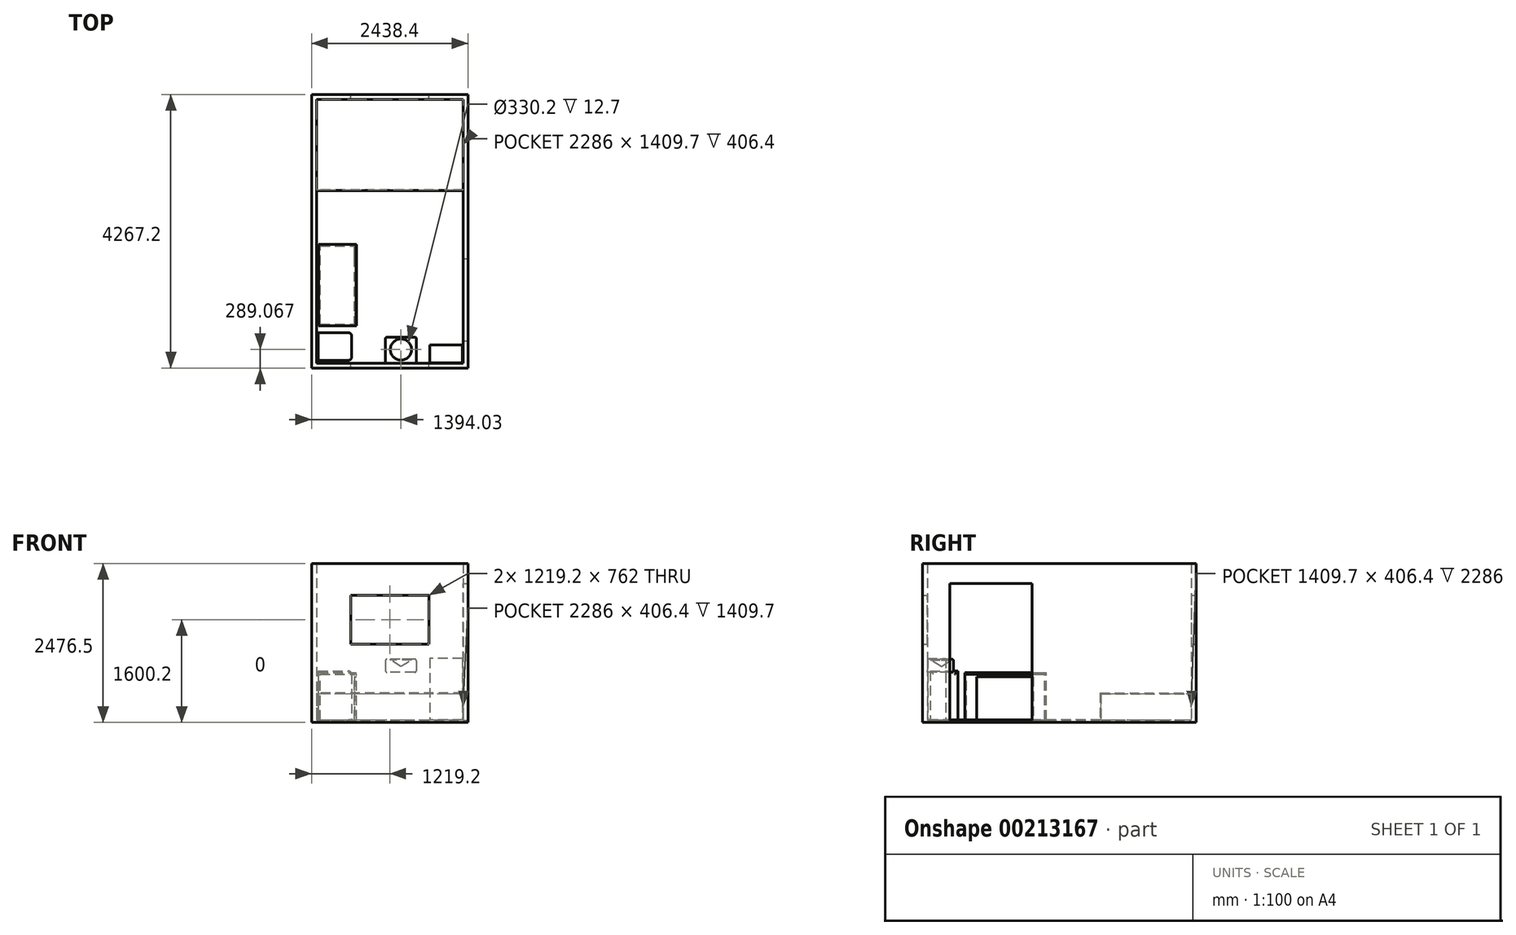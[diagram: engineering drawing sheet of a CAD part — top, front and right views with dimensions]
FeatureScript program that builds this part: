
annotation { "Feature Type Name" : "Feature", "Feature Type Description" : "" }
export const myFeature = defineFeature(function(context is Context, id is Id, definition is map)
    precondition{}
    {
        {
            var Q0;
            Q0=qCreatedBy(makeId("Top.planeOp"),FACE);
            var sketch = newSketch(context, id + "F0", { "sketchPlane" : qUnion([Q0])});
            skLineSegment(sketch, "E0.bottom", {"start": v(0, 0) * mm, "end": v(2438.4, 0) * mm});
            skLineSegment(sketch, "E0.top", {"start": v(0, 4267.2) * mm, "end": v(2438.4, 4267.2) * mm});
            skLineSegment(sketch, "E0.left", {"start": v(0, 0) * mm, "end": v(0, 4267.2) * mm});
            skLineSegment(sketch, "E0.right", {"start": v(2438.4, 0) * mm, "end": v(2438.4, 4267.2) * mm});
            skSolve(sketch);
        }
        {
            var Q0;
            Q0=makeQuery(id+"F0.imprint","IMPRINT",FACE,{"disambiguationData":[TD([[makeQuery(id+"F0.imprint","IMPRINT",EDGE,{"derivedFrom":sQuery(id+"F0.wireOp",EDGE,"E0.bottom")}),1.0]])]});
            extrude(context, id + "F1", {"entities" : qUnion([Q0]), "depth" : 38.1 * mm});
        }
        {
            var Q0;
            Q0=makeQuery(id+"F1.opExtrude","CAP_FACE",FACE,{"disambiguationData":[OSD([sQuery(id+"F0.wireOp",EDGE,"E0.bottom"),sQuery(id+"F0.wireOp",EDGE,"E0.top"),sQuery(id+"F0.wireOp",EDGE,"E0.left"),sQuery(id+"F0.wireOp",EDGE,"E0.right")])],"isStart":false});
            var sketch = newSketch(context, id + "F2", { "sketchPlane" : qUnion([Q0])});
            skLineSegment(sketch, "E1.bottom", {"start": v(0, 0) * mm, "end": v(2438.4, 0) * mm});
            skLineSegment(sketch, "E1.top", {"start": v(76.2, 76.2) * mm, "end": v(2362.2, 76.2) * mm});
            skLineSegment(sketch, "E1.left", {"start": v(0, 0) * mm, "end": v(0, 76.2) * mm});
            skLineSegment(sketch, "E1.right", {"start": v(2438.4, 0) * mm, "end": v(2438.4, 76.2) * mm});
            skLineSegment(sketch, "E2.bottom", {"start": v(2438.4, 0) * mm, "end": v(2362.2, 0) * mm});
            skLineSegment(sketch, "E2.top", {"start": v(2438.4, 4267.2) * mm, "end": v(2362.2, 4267.2) * mm});
            skLineSegment(sketch, "E2.left", {"start": v(2438.4, 0) * mm, "end": v(2438.4, 4267.2) * mm});
            skLineSegment(sketch, "E2.right", {"start": v(2362.2, 76.2) * mm, "end": v(2362.2, 4191) * mm});
            skLineSegment(sketch, "E3.bottom", {"start": v(2438.4, 4267.2) * mm, "end": v(0, 4267.2) * mm});
            skLineSegment(sketch, "E3.top", {"start": v(2362.2, 4191) * mm, "end": v(76.2, 4191) * mm});
            skLineSegment(sketch, "E3.left", {"start": v(2438.4, 4267.2) * mm, "end": v(2438.4, 4191) * mm});
            skLineSegment(sketch, "E3.right", {"start": v(0, 4267.2) * mm, "end": v(0, 4191) * mm});
            skLineSegment(sketch, "E4.bottom", {"start": v(0, 4267.2) * mm, "end": v(76.2, 4267.2) * mm});
            skLineSegment(sketch, "E4.top", {"start": v(0, 0) * mm, "end": v(76.2, 0) * mm});
            skLineSegment(sketch, "E4.left", {"start": v(0, 4267.2) * mm, "end": v(0, 0) * mm});
            skLineSegment(sketch, "E4.right", {"start": v(76.2, 4191) * mm, "end": v(76.2, 76.2) * mm});
            skSolve(sketch);
        }
        {
            var Q0;
            Q0=makeQuery(id+"F2.imprint","IMPRINT",FACE,{"disambiguationData":[TD([[makeQuery(id+"F2.imprint","IMPRINT",EDGE,{"derivedFrom":sQuery(id+"F2.wireOp",EDGE,"E1.bottom")}),1.0]])]});
            extrude(context, id + "F3", {"entities" : qUnion([Q0]), "operationType" : NewBodyOperationType.ADD, "depth" : 2438.4 * mm});
        }
        {
            var Q0;
            Q0=makeQuery(id+"F3.boolean.opBoolean","MERGE",FACE,{"derivedFrom":[makeQuery(id+"F1.opExtrude","SWEPT_FACE",FACE,{"disambiguationData":[OSD([sQuery(id+"F0.wireOp",EDGE,"E0.right")])]}),makeQuery(id+"F3.opExtrude","SWEPT_FACE",FACE,{"disambiguationData":[OSD([sQuery(id+"F2.wireOp",EDGE,"E2.left"),sQuery(id+"F2.wireOp",EDGE,"E3.left")])]})]});
            var sketch = newSketch(context, id + "F4", { "sketchPlane" : qUnion([Q0])});
            skLineSegment(sketch, "E5.bottom", {"start": v(0, 0) * mm, "end": v(422.77, 0) * mm});
            skLineSegment(sketch, "E5.left", {"start": v(0, 0) * mm, "end": v(0, 35.23) * mm});
            skLineSegment(sketch, "E6.bottom", {"start": v(422.77, 35.23) * mm, "end": v(1708.3, 35.23) * mm});
            skLineSegment(sketch, "E6.top", {"start": v(422.77, 2168.83) * mm, "end": v(1708.3, 2168.83) * mm});
            skLineSegment(sketch, "E6.left", {"start": v(422.77, 35.23) * mm, "end": v(422.77, 2168.83) * mm});
            skLineSegment(sketch, "E6.right", {"start": v(1708.3, 35.23) * mm, "end": v(1708.3, 2168.83) * mm});
            skSolve(sketch);
        }
        {
            var Q0;
            Q0 = qSketchRegion(id + "F4", true);
            extrude(context, id + "F5", {"entities" : qUnion([Q0]), "operationType" : NewBodyOperationType.REMOVE, "oppositeDirection" : true, "depth" : 76.2 * mm});
        }
        {
            var Q0;
            Q0=makeQuery(id+"F3.boolean.opBoolean","MERGE",FACE,{"derivedFrom":[makeQuery(id+"F1.opExtrude","SWEPT_FACE",FACE,{"disambiguationData":[OSD([sQuery(id+"F0.wireOp",EDGE,"E0.top")])]}),makeQuery(id+"F3.opExtrude","SWEPT_FACE",FACE,{"disambiguationData":[OSD([sQuery(id+"F2.wireOp",EDGE,"E3.bottom"),sQuery(id+"F2.wireOp",EDGE,"E4.bottom")])]})]});
            var sketch = newSketch(context, id + "F6", { "sketchPlane" : qUnion([Q0])});
            skLineSegment(sketch, "E7.bottom", {"start": v(-1828.8, 1219.2) * mm, "end": v(-609.6, 1219.2) * mm});
            skLineSegment(sketch, "E7.top", {"start": v(-1828.8, 1981.2) * mm, "end": v(-609.6, 1981.2) * mm});
            skLineSegment(sketch, "E7.left", {"start": v(-1828.8, 1219.2) * mm, "end": v(-1828.8, 1981.2) * mm});
            skLineSegment(sketch, "E7.right", {"start": v(-609.6, 1219.2) * mm, "end": v(-609.6, 1981.2) * mm});
            skSolve(sketch);
        }
        {
            var Q0;
            Q0 = qSketchRegion(id + "F6", true);
            extrude(context, id + "F7", {"entities" : qUnion([Q0]), "operationType" : NewBodyOperationType.REMOVE, "oppositeDirection" : true, "depth" : 4996.18 * mm});
        }
        {
            var Q0;
            Q0=makeQuery(id+"F1.opExtrude","CAP_FACE",FACE,{"disambiguationData":[OSD([sQuery(id+"F0.wireOp",EDGE,"E0.bottom"),sQuery(id+"F0.wireOp",EDGE,"E0.top"),sQuery(id+"F0.wireOp",EDGE,"E0.left"),sQuery(id+"F0.wireOp",EDGE,"E0.right")])],"isStart":false});
            var sketch = newSketch(context, id + "F8", { "sketchPlane" : qUnion([Q0])});
            skLineSegment(sketch, "E8", {"start": v(76.2, 4191) * mm, "end": v(76.2, 2768.6) * mm});
            skLineSegment(sketch, "E9", {"start": v(76.2, 2768.6) * mm, "end": v(2362.2, 2768.6) * mm});
            skLineSegment(sketch, "E10", {"start": v(2362.2, 2768.6) * mm, "end": v(2362.2, 2781.3) * mm});
            skLineSegment(sketch, "E11", {"start": v(2362.2, 2781.3) * mm, "end": v(76.2, 2781.3) * mm});
            skLineSegment(sketch, "E12", {"start": v(76.2, 2781.3) * mm, "end": v(76.2, 2768.6) * mm});
            skSolve(sketch);
        }
        {
            var Q0;
            Q0=makeQuery(id+"F8.imprint","IMPRINT",FACE,{"disambiguationData":[TD([[makeQuery(id+"F8.imprint","IMPRINT",EDGE,{"derivedFrom":sQuery(id+"F8.wireOp",EDGE,"E9")}),1.0]])]});
            extrude(context, id + "F9", {"entities" : qUnion([Q0]), "operationType" : NewBodyOperationType.ADD, "depth" : 406.4 * mm});
        }
        {
            var Q0;
            Q0=makeQuery(id+"F9.opExtrude","CAP_FACE",FACE,{"disambiguationData":[OSD([sQuery(id+"F8.wireOp",EDGE,"E9"),sQuery(id+"F8.wireOp",EDGE,"E10"),sQuery(id+"F8.wireOp",EDGE,"E11"),sQuery(id+"F8.wireOp",EDGE,"E12")])],"isStart":false});
            var sketch = newSketch(context, id + "F10", { "sketchPlane" : qUnion([Q0])});
            skLineSegment(sketch, "E13.bottom", {"start": v(76.2, 2768.6) * mm, "end": v(2362.3, 2768.6) * mm});
            skLineSegment(sketch, "E13.top", {"start": v(76.2, 4191.12) * mm, "end": v(2362.3, 4191.12) * mm});
            skLineSegment(sketch, "E13.left", {"start": v(76.2, 2768.6) * mm, "end": v(76.2, 4191.12) * mm});
            skLineSegment(sketch, "E13.right", {"start": v(2362.3, 2768.6) * mm, "end": v(2362.3, 4191.12) * mm});
            skSolve(sketch);
        }
        {
            var Q0;
            Q0 = qSketchRegion(id + "F10", true);
            extrude(context, id + "F11", {"entities" : qUnion([Q0]), "operationType" : NewBodyOperationType.ADD, "depth" : 12.7 * mm});
        }
        {
            var Q0;
            {var subQ3=sQuery(id+"F8.wireOp",EDGE,"E9");Q0=makeQuery(id+"F8.imprint","IMPRINT",FACE,{"disambiguationData":[TD([[makeQuery(id+"F8.imprint","IMPRINT",EDGE,{"derivedFrom":subQ3}),-1.0]])]});}
            var sketch = newSketch(context, id + "F12", { "sketchPlane" : qUnion([Q0])});
            skLineSegment(sketch, "E14.bottom", {"start": v(103.72, 120.24) * mm, "end": v(624.42, 120.24) * mm});
            skLineSegment(sketch, "E14.top", {"start": v(103.72, 552.04) * mm, "end": v(624.42, 552.04) * mm});
            skLineSegment(sketch, "E14.left", {"start": v(103.72, 120.24) * mm, "end": v(103.72, 552.04) * mm});
            skLineSegment(sketch, "E14.right", {"start": v(624.42, 120.24) * mm, "end": v(624.42, 552.04) * mm});
            skSolve(sketch);
        }
        {
            var Q0;
            Q0=makeQuery(id+"F12.imprint","IMPRINT",FACE,{"disambiguationData":[TD([[makeQuery(id+"F12.imprint","IMPRINT",EDGE,{"derivedFrom":sQuery(id+"F12.wireOp",EDGE,"E14.bottom")}),1.0]])]});
            extrude(context, id + "F13", {"entities" : qUnion([Q0]), "operationType" : NewBodyOperationType.ADD, "depth" : 762 * mm});
        }
        {
            var Q0;
            Q0=makeQuery(id+"F3.opExtrude","SWEPT_FACE",FACE,{"disambiguationData":[OSD([sQuery(id+"F2.wireOp",EDGE,"E1.top")])]});
            var sketch = newSketch(context, id + "F14", { "sketchPlane" : qUnion([Q0])});
            skLineSegment(sketch, "E15.bottom", {"start": v(-1634.48, 985.27) * mm, "end": v(-1151.88, 985.27) * mm});
            skLineSegment(sketch, "E15.top", {"start": v(-1634.48, 782.07) * mm, "end": v(-1151.88, 782.07) * mm});
            skLineSegment(sketch, "E15.left", {"start": v(-1634.48, 985.27) * mm, "end": v(-1634.48, 782.07) * mm});
            skLineSegment(sketch, "E15.right", {"start": v(-1151.88, 985.27) * mm, "end": v(-1151.88, 782.07) * mm});
            skSolve(sketch);
        }
        {
            var Q0;
            Q0=makeQuery(id+"F14.imprint","IMPRINT",FACE,{"disambiguationData":[TD([[makeQuery(id+"F14.imprint","IMPRINT",EDGE,{"derivedFrom":sQuery(id+"F14.wireOp",EDGE,"E15.bottom")}),-1.0]])]});
            extrude(context, id + "F15", {"entities" : qUnion([Q0]), "operationType" : NewBodyOperationType.ADD, "depth" : 406.4 * mm});
        }
        {
            var Q0;
            Q0=makeQuery(id+"F15.opExtrude","SWEPT_FACE",FACE,{"disambiguationData":[OSD([sQuery(id+"F14.wireOp",EDGE,"E15.bottom")])]});
            var sketch = newSketch(context, id + "F16", { "sketchPlane" : qUnion([Q0])});
            skCircle(sketch, "E16", {"center": v(1394.03, 289.07) * mm, "radius": 114.3 * mm});
            skSolve(sketch);
        }
        {
            var Q0;
            Q0=sQuery(id+"F16.wireOp",VERTEX,"E16.center");
            var Q1;
            Q1=makeQuery(id+"F1.opExtrude","SWEPT_BODY",BODY,{"disambiguationData":[OSD([sQuery(id+"F0.wireOp",EDGE,"E0.bottom"),sQuery(id+"F0.wireOp",EDGE,"E0.top"),sQuery(id+"F0.wireOp",EDGE,"E0.left"),sQuery(id+"F0.wireOp",EDGE,"E0.right")])]});
            hole(context, id + "F17", {"style" : HoleStyle.SIMPLE, "endStyle" : HoleEndStyle.BLIND, "holeDiameter" : 330.2 * mm, "holeDepth" : 12.7 * mm, "locations" : qUnion([Q0]), "scope" : qUnion([Q1])});
        }
        {
            var Q0;
            Q0=makeQuery(id+"F15.opExtrude","SWEPT_EDGE",EDGE,{"disambiguationData":[OSD([sQuery(id+"F14.wireOp",EDGE,"E15.bottom"),sQuery(id+"F14.wireOp",EDGE,"E15.left")])]});
            var Q1;
            Q1=makeQuery(id+"F15.opExtrude","SWEPT_EDGE",EDGE,{"disambiguationData":[OSD([sQuery(id+"F14.wireOp",EDGE,"E15.bottom"),sQuery(id+"F14.wireOp",EDGE,"E15.right")])]});
            var Q2;
            Q2=makeQuery(id+"F15.opExtrude","CAP_EDGE",EDGE,{"disambiguationData":[OSD([sQuery(id+"F14.wireOp",EDGE,"E15.right")])],"isStart":false});
            var Q3;
            Q3=makeQuery(id+"F15.opExtrude","CAP_EDGE",EDGE,{"disambiguationData":[OSD([sQuery(id+"F14.wireOp",EDGE,"E15.left")])],"isStart":false});
            var Q4;
            Q4=makeQuery(id+"F15.opExtrude","CAP_EDGE",EDGE,{"disambiguationData":[OSD([sQuery(id+"F14.wireOp",EDGE,"E15.top")])],"isStart":false});
            var Q5;
            Q5=makeQuery(id+"F15.opExtrude","SWEPT_EDGE",EDGE,{"disambiguationData":[OSD([sQuery(id+"F14.wireOp",EDGE,"E15.top"),sQuery(id+"F14.wireOp",EDGE,"E15.left")])]});
            var Q6;
            Q6=makeQuery(id+"F15.opExtrude","SWEPT_EDGE",EDGE,{"disambiguationData":[OSD([sQuery(id+"F14.wireOp",EDGE,"E15.top"),sQuery(id+"F14.wireOp",EDGE,"E15.right")])]});
            var Q7;
            Q7=makeQuery(id+"F15.opExtrude","CAP_EDGE",EDGE,{"disambiguationData":[OSD([sQuery(id+"F14.wireOp",EDGE,"E15.bottom")])],"isStart":false});
            fillet(context, id + "F18", {"entities" : qUnion([Q0, Q1, Q2, Q3, Q4, Q5, Q6, Q7]), "radius" : 25.4 * mm, "tangentPropagation" : true, "allowEdgeOverflow" : false});
        }
        {
            var Q0;
            Q0=makeQuery(id+"F13.opExtrude","CAP_EDGE",EDGE,{"disambiguationData":[OSD([sQuery(id+"F12.wireOp",EDGE,"E14.right")])],"isStart":false});
            var Q1;
            Q1=makeQuery(id+"F13.opExtrude","SWEPT_EDGE",EDGE,{"disambiguationData":[OSD([sQuery(id+"F12.wireOp",EDGE,"E14.top"),sQuery(id+"F12.wireOp",EDGE,"E14.right")])]});
            var Q2;
            Q2=makeQuery(id+"F13.opExtrude","SWEPT_EDGE",EDGE,{"disambiguationData":[OSD([sQuery(id+"F12.wireOp",EDGE,"E14.bottom"),sQuery(id+"F12.wireOp",EDGE,"E14.right")])]});
            fillet(context, id + "F19", {"entities" : qUnion([Q0, Q1, Q2]), "radius" : 50.8 * mm, "tangentPropagation" : true, "allowEdgeOverflow" : false});
        }
        {
            var Q0;
            {var subQ3=sQuery(id+"F8.wireOp",EDGE,"E9");Q0=makeQuery(id+"F8.imprint","IMPRINT",FACE,{"disambiguationData":[TD([[makeQuery(id+"F8.imprint","IMPRINT",EDGE,{"derivedFrom":subQ3}),-1.0]])]});}
            var sketch = newSketch(context, id + "F20", { "sketchPlane" : qUnion([Q0])});
            skLineSegment(sketch, "E17.bottom", {"start": v(136.23, 659.12) * mm, "end": v(695.03, 659.12) * mm});
            skLineSegment(sketch, "E17.top", {"start": v(136.23, 1929.12) * mm, "end": v(695.03, 1929.12) * mm});
            skLineSegment(sketch, "E17.left", {"start": v(136.23, 659.12) * mm, "end": v(136.23, 1929.12) * mm});
            skLineSegment(sketch, "E17.right", {"start": v(695.03, 659.12) * mm, "end": v(695.03, 1929.12) * mm});
            skSolve(sketch);
        }
        {
            var Q0;
            Q0=sQuery(id+"F20.wireOp",EDGE,"E17.top");
            var Q1;
            Q1=sQuery(id+"F20.wireOp",EDGE,"E17.right");
            var Q2;
            Q2=sQuery(id+"F20.wireOp",EDGE,"E17.left");
            var Q3;
            Q3=sQuery(id+"F20.wireOp",EDGE,"E17.bottom");
            extrude(context, id + "F21", {"bodyType" : ToolBodyType.SURFACE, "surfaceEntities" : qUnion([Q0, Q1, Q2, Q3]), "depth" : 711.2 * mm});
        }
        {
            var Q0;
            Q0=makeQuery(id+"F21.opExtrude","SWEPT_FACE",FACE,{"disambiguationData":[OSD([sQuery(id+"F20.wireOp",EDGE,"E17.right")])]});
            var Q1;
            Q1=makeQuery(id+"F21.opExtrude","SWEPT_FACE",FACE,{"disambiguationData":[OSD([sQuery(id+"F20.wireOp",EDGE,"E17.left")])]});
            extrude(context, id + "F22", {"entities" : qUnion([Q0, Q1]), "operationType" : NewBodyOperationType.ADD, "depth" : 25.4 * mm});
        }
        {
            var Q0;
            Q0=makeQuery(id+"F21.opExtrude","SWEPT_FACE",FACE,{"disambiguationData":[OSD([sQuery(id+"F20.wireOp",EDGE,"E17.top")])]});
            var sketch = newSketch(context, id + "F23", { "sketchPlane" : qUnion([Q0])});
            skLineSegment(sketch, "E18.bottom", {"start": v(136.23, 38.1) * mm, "end": v(695.03, 38.1) * mm});
            skLineSegment(sketch, "E18.top", {"start": v(136.23, 749.3) * mm, "end": v(695.03, 749.3) * mm});
            skLineSegment(sketch, "E18.left", {"start": v(136.23, 38.1) * mm, "end": v(136.23, 749.3) * mm});
            skLineSegment(sketch, "E18.right", {"start": v(695.03, 38.1) * mm, "end": v(695.03, 749.3) * mm});
            skSolve(sketch);
        }
        {
            var Q0;
            Q0=makeQuery(id+"F23.imprint","IMPRINT",FACE,{"disambiguationData":[TD([[makeQuery(id+"F23.imprint","IMPRINT",EDGE,{"derivedFrom":sQuery(id+"F23.wireOp",EDGE,"E18.bottom")}),1.0]])]});
            extrude(context, id + "F24", {"entities" : qUnion([Q0]), "operationType" : NewBodyOperationType.ADD, "depth" : 25.4 * mm});
        }
        {
            var Q0;
            Q0=makeQuery(id+"F21.opExtrude","SWEPT_FACE",FACE,{"disambiguationData":[OSD([sQuery(id+"F20.wireOp",EDGE,"E17.bottom")])]});
            var sketch = newSketch(context, id + "F25", { "sketchPlane" : qUnion([Q0])});
            skLineSegment(sketch, "E19.bottom", {"start": v(-136.23, 38.1) * mm, "end": v(-669.09, 38.1) * mm});
            skLineSegment(sketch, "E19.top", {"start": v(-136.23, 749.3) * mm, "end": v(-669.09, 749.3) * mm});
            skLineSegment(sketch, "E19.left", {"start": v(-136.23, 38.1) * mm, "end": v(-136.23, 749.3) * mm});
            skLineSegment(sketch, "E19.right", {"start": v(-669.09, 38.1) * mm, "end": v(-669.09, 749.3) * mm});
            skSolve(sketch);
        }
        {
            var Q0;
            Q0 = qSketchRegion(id + "F25", true);
            extrude(context, id + "F26", {"entities" : qUnion([Q0]), "operationType" : NewBodyOperationType.ADD, "depth" : 25.4 * mm});
        }
        {
            var Q0;
            {var subQ0=sQuery(id+"F20.wireOp",EDGE,"E17.right");var subQ1=sQuery(id+"F20.wireOp",EDGE,"E17.left");Q0=makeQuery(id+"F26.boolean.opBoolean","MERGE",FACE,{"derivedFrom":[makeQuery(id+"F24.boolean.opBoolean","MERGE",FACE,{"derivedFrom":[makeQuery(id+"F22.opExtrude","SWEPT_FACE",FACE,{"disambiguationData":[OSD([subQ1]),TDD([makeQuery(id+"F21.opExtrude","CAP_EDGE",EDGE,{"disambiguationData":[OSD([subQ1])],"isStart":false})])]}),makeQuery(id+"F22.opExtrude","SWEPT_FACE",FACE,{"disambiguationData":[OSD([subQ0]),TDD([makeQuery(id+"F21.opExtrude","CAP_EDGE",EDGE,{"disambiguationData":[OSD([subQ0])],"isStart":false})])]}),makeQuery(id+"F24.opExtrude","SWEPT_FACE",FACE,{"disambiguationData":[OSD([sQuery(id+"F23.wireOp",EDGE,"E18.top")])]})]}),makeQuery(id+"F26.opExtrude","SWEPT_FACE",FACE,{"disambiguationData":[OSD([sQuery(id+"F25.wireOp",EDGE,"E19.top")])]})]});}
            var sketch = newSketch(context, id + "F27", { "sketchPlane" : qUnion([Q0])});
            skLineSegment(sketch, "E20.bottom", {"start": v(110.83, 1929.12) * mm, "end": v(695.03, 1929.12) * mm});
            skLineSegment(sketch, "E20.top", {"start": v(110.83, 659.12) * mm, "end": v(695.03, 659.12) * mm});
            skLineSegment(sketch, "E20.left", {"start": v(110.83, 1929.12) * mm, "end": v(110.83, 659.12) * mm});
            skLineSegment(sketch, "E20.right", {"start": v(695.03, 1929.12) * mm, "end": v(695.03, 659.12) * mm});
            skSolve(sketch);
        }
        {
            var Q0;
            Q0 = qSketchRegion(id + "F27", true);
            extrude(context, id + "F28", {"entities" : qUnion([Q0]), "operationType" : NewBodyOperationType.ADD, "depth" : 25.4 * mm});
        }
        {
            var Q0;
            Q0=makeQuery(id+"F21.opExtrude","SWEPT_FACE",FACE,{"disambiguationData":[OSD([sQuery(id+"F20.wireOp",EDGE,"E17.right")])]});
            var sketch = newSketch(context, id + "F29", { "sketchPlane" : qUnion([Q0])});
            skLineSegment(sketch, "E21.bottom", {"start": v(-659.12, 38.1) * mm, "end": v(-1929.12, 38.1) * mm});
            skLineSegment(sketch, "E21.top", {"start": v(-659.12, 749.3) * mm, "end": v(-1929.12, 749.3) * mm});
            skLineSegment(sketch, "E21.left", {"start": v(-659.12, 38.1) * mm, "end": v(-659.12, 749.3) * mm});
            skLineSegment(sketch, "E21.right", {"start": v(-1929.12, 38.1) * mm, "end": v(-1929.12, 749.3) * mm});
            skSolve(sketch);
        }
        {
            var Q0;
            Q0 = qSketchRegion(id + "F29", true);
            extrude(context, id + "F30", {"entities" : qUnion([Q0]), "operationType" : NewBodyOperationType.ADD, "oppositeDirection" : true, "depth" : 6.86 * mm});
        }
        {
            var Q0;
            Q0=makeQuery(id+"F30.opExtrude","CAP_FACE",FACE,{"disambiguationData":[OSD([sQuery(id+"F29.wireOp",EDGE,"E21.bottom"),sQuery(id+"F29.wireOp",EDGE,"E21.top"),sQuery(id+"F29.wireOp",EDGE,"E21.left"),sQuery(id+"F29.wireOp",EDGE,"E21.right")])],"isStart":false});
            var sketch = newSketch(context, id + "F31", { "sketchPlane" : qUnion([Q0])});
            skLineSegment(sketch, "E22.bottom", {"start": v(846.24, 38.1) * mm, "end": v(1728.94, 38.1) * mm});
            skLineSegment(sketch, "E22.top", {"start": v(846.24, 711.24) * mm, "end": v(1728.94, 711.24) * mm});
            skLineSegment(sketch, "E22.left", {"start": v(846.24, 38.1) * mm, "end": v(846.24, 711.24) * mm});
            skLineSegment(sketch, "E22.right", {"start": v(1728.94, 38.1) * mm, "end": v(1728.94, 711.24) * mm});
            skSolve(sketch);
        }
        {
            var Q0;
            Q0 = qSketchRegion(id + "F31", true);
            extrude(context, id + "F32", {"entities" : qUnion([Q0]), "operationType" : NewBodyOperationType.REMOVE, "oppositeDirection" : true, "depth" : 76.2 * mm});
        }
        {
            var Q0;
            {var subQ3=sQuery(id+"F8.wireOp",EDGE,"E9");Q0=makeQuery(id+"F8.imprint","IMPRINT",FACE,{"disambiguationData":[TD([[makeQuery(id+"F8.imprint","IMPRINT",EDGE,{"derivedFrom":subQ3}),-1.0]])]});}
            var sketch = newSketch(context, id + "F33", { "sketchPlane" : qUnion([Q0])});
            skLineSegment(sketch, "E23.bottom", {"start": v(2351.64, 80.65) * mm, "end": v(1843.64, 80.65) * mm});
            skLineSegment(sketch, "E23.top", {"start": v(2351.64, 360.05) * mm, "end": v(1843.64, 360.05) * mm});
            skLineSegment(sketch, "E23.left", {"start": v(2351.64, 80.65) * mm, "end": v(2351.64, 360.05) * mm});
            skLineSegment(sketch, "E23.right", {"start": v(1843.64, 80.65) * mm, "end": v(1843.64, 360.05) * mm});
            skSolve(sketch);
        }
        {
            var Q0;
            Q0 = qSketchRegion(id + "F33", true);
            extrude(context, id + "F34", {"entities" : qUnion([Q0]), "operationType" : NewBodyOperationType.ADD, "depth" : 957.58 * mm});
        }
    });
